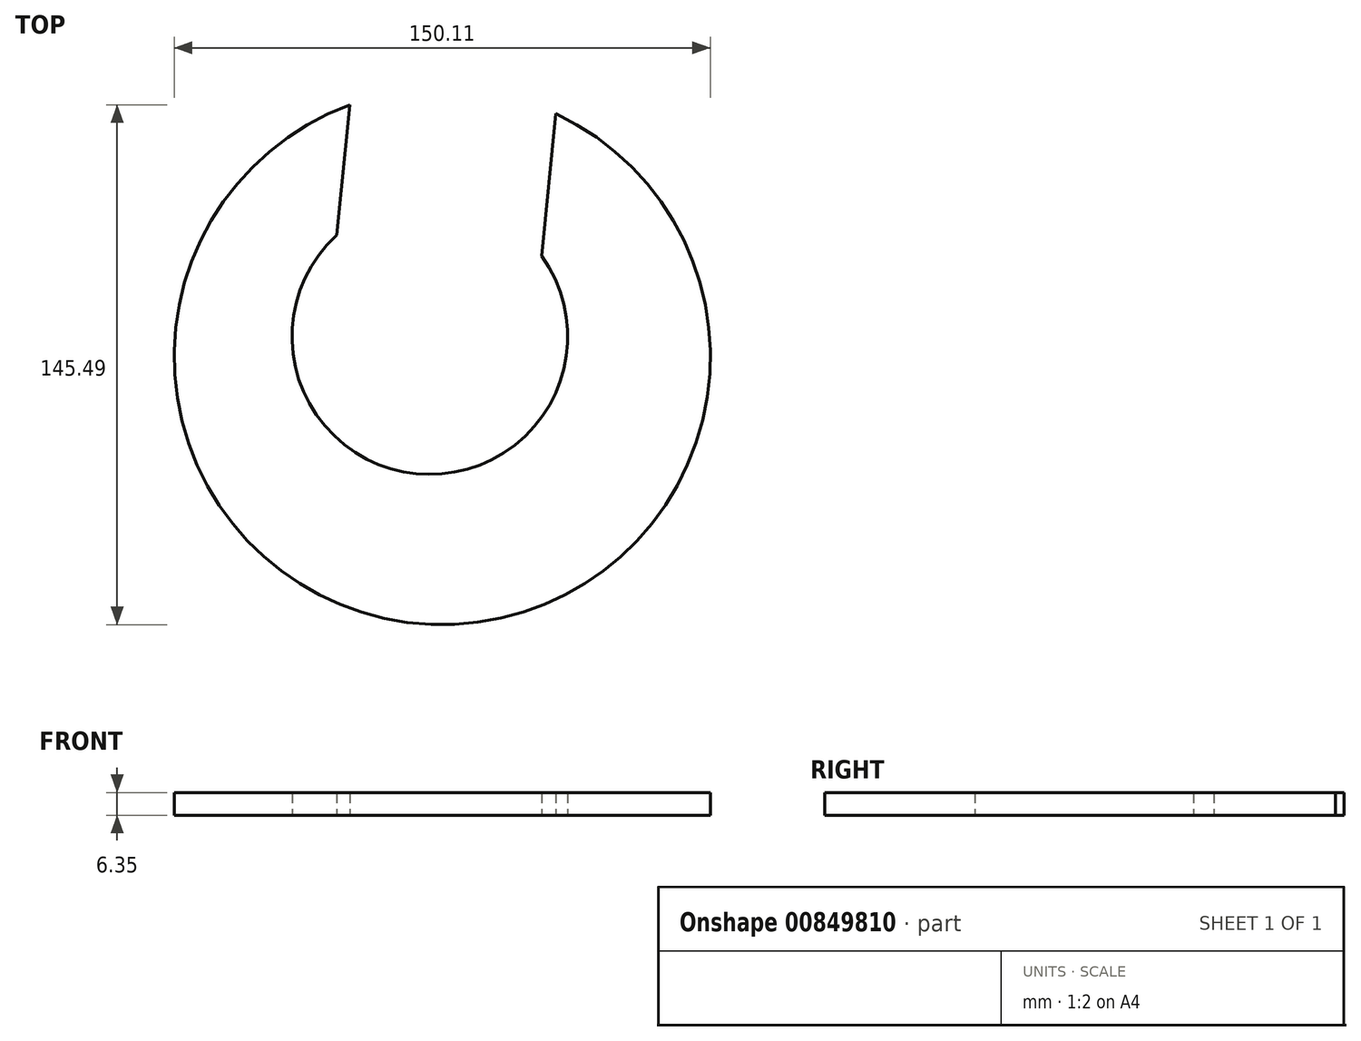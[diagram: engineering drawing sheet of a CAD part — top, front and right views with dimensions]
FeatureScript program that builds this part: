
annotation { "Feature Type Name" : "Feature", "Feature Type Description" : "" }
export const myFeature = defineFeature(function(context is Context, id is Id, definition is map)
    precondition{}
    {
        {
            var Q0;
            Q0=qCreatedBy(makeId("Top.planeOp"),FACE);
            var sketch = newSketch(context, id + "F0", { "sketchPlane" : qUnion([Q0])});
            skArc(sketch, "E0", {"start": v(-25.2, 65.6) * mm, "mid": v(-2.44, -79.82) * mm, "end": v(32.52, 63.17) * mm});
            skLineSegment(sketch, "E1", {"start": v(32.52, 63.17) * mm, "end": v(28.55, 23.36) * mm});
            skLineSegment(sketch, "E2", {"start": v(-25.2, 65.6) * mm, "end": v(-28.86, 29.16) * mm});
            skArc(sketch, "E3", {"start": v(-28.86, 29.16) * mm, "mid": v(-6.6, -37.62) * mm, "end": v(28.55, 23.36) * mm});
            skSolve(sketch);
        }
        {
            var Q0;
            Q0=makeQuery(id+"F0.imprint","IMPRINT",FACE,{"disambiguationData":[TD([[makeQuery(id+"F0.imprint","IMPRINT",EDGE,{"derivedFrom":sQuery(id+"F0.wireOp",EDGE,"E0")}),1.0]])]});
            extrude(context, id + "F1", {"entities" : qUnion([Q0]), "depth" : 6.35 * mm, "offsetDistance" : 25.4 * mm});
        }
    });
